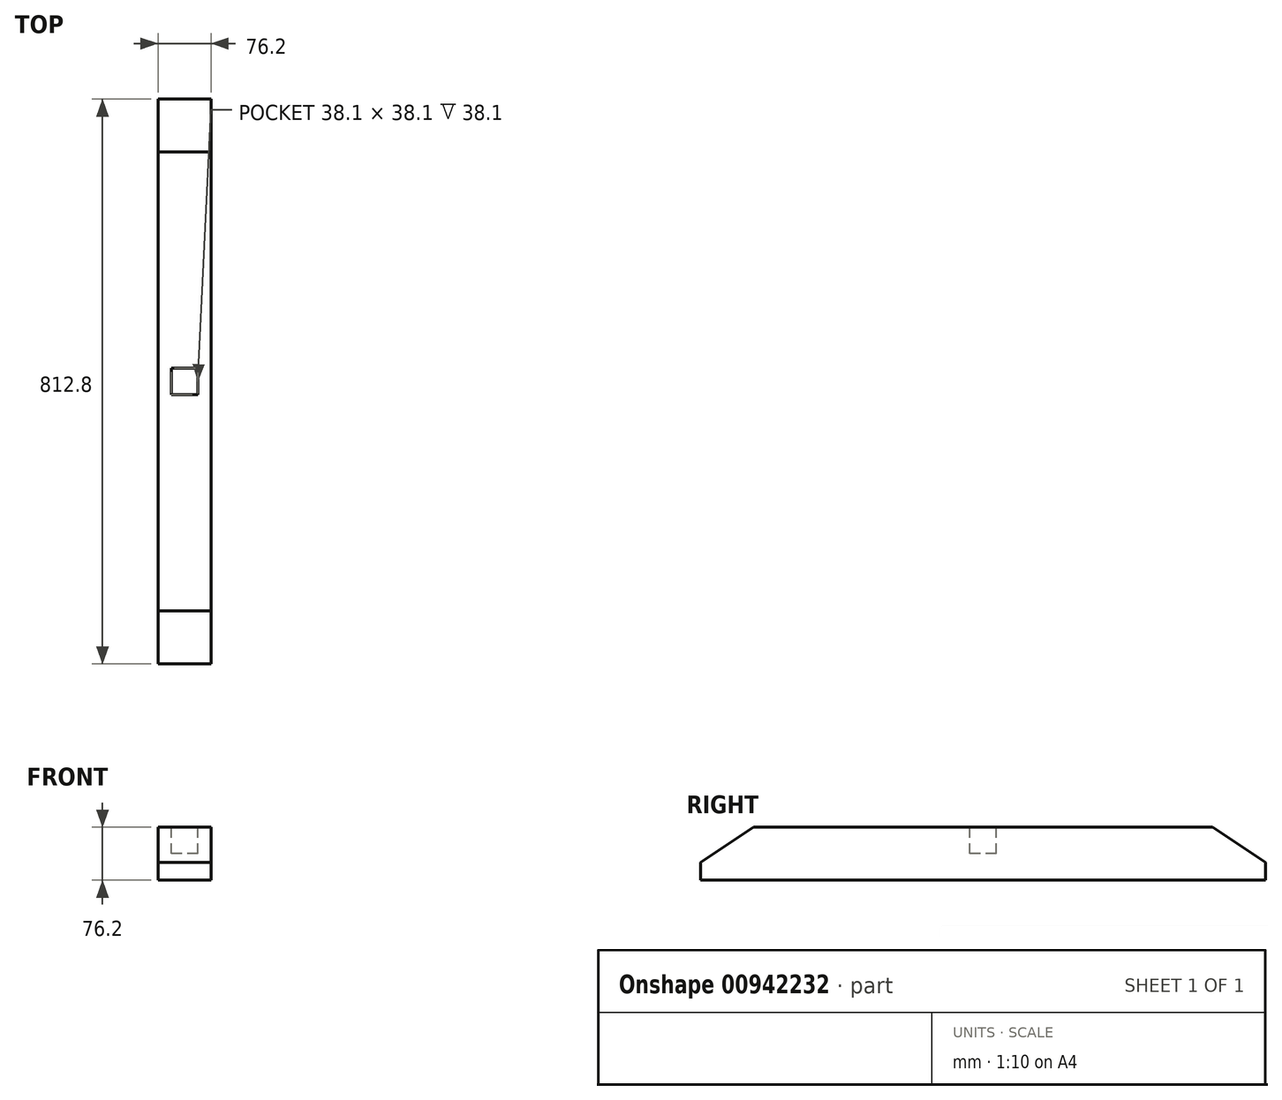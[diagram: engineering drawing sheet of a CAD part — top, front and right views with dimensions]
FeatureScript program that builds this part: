
annotation { "Feature Type Name" : "Feature", "Feature Type Description" : "" }
export const myFeature = defineFeature(function(context is Context, id is Id, definition is map)
    precondition{}
    {
        {
            var Q0;
            Q0=qCreatedBy(makeId("Right.planeOp"),FACE);
            var sketch = newSketch(context, id + "F0", { "sketchPlane" : qUnion([Q0])});
            skLineSegment(sketch, "E0.bottom", {"start": v(330.2, 38.1) * mm, "end": v(-330.2, 38.1) * mm});
            skLineSegment(sketch, "E0.top", {"start": v(406.4, -38.1) * mm, "end": v(292.1, -38.1) * mm});
            skLineSegment(sketch, "E0.left", {"start": v(406.4, -12.7) * mm, "end": v(406.4, -38.1) * mm});
            skLineSegment(sketch, "E0.right", {"start": v(-406.4, -12.7) * mm, "end": v(-406.4, -38.1) * mm});
            skPoint(sketch, "E0.middle", {"position": v(0, 0) * mm});
            skPoint(sketch, "E1.middle", {"position": v(0, -38.1) * mm});
            skLineSegment(sketch, "E2.trimOffspring", {"start": v(-292.1, -38.1) * mm, "end": v(-406.4, -38.1) * mm});
            skPoint(sketch, "E3.orphan", {"position": v(292.1, -57.15) * mm});
            skPoint(sketch, "E4.orphan", {"position": v(-292.1, -57.15) * mm});
            skLineSegment(sketch, "E5", {"start": v(-406.4, -38.1) * mm, "end": v(-406.4, -12.7) * mm});
            skLineSegment(sketch, "E6", {"start": v(-406.4, -12.7) * mm, "end": v(-330.2, 38.1) * mm});
            skLineSegment(sketch, "E7.MirrorCS", {"start": v(406.4, -12.7) * mm, "end": v(330.2, 38.1) * mm});
            skPoint(sketch, "E8.orphan", {"position": v(-406.4, 38.1) * mm});
            skPoint(sketch, "E9.orphan", {"position": v(406.4, 38.1) * mm});
            skLineSegment(sketch, "E10", {"start": v(-292.1, -38.1) * mm, "end": v(292.1, -38.1) * mm});
            skPoint(sketch, "E1.right.start.orphan", {"position": v(-292.1, -19.05) * mm});
            skPoint(sketch, "E1.left.start.orphan", {"position": v(292.1, -19.05) * mm});
            skSolve(sketch);
        }
        {
            var Q0;
            Q0=qSketchRegion(id+"F0",true);
            extrude(context, id + "F1", {"entities" : qUnion([Q0]), "depth" : 76.2 * mm, "offsetDistance" : 25.4 * mm});
        }
        {
            var Q0;
            Q0=makeQuery(id+"F1.opExtrude","SWEPT_FACE",FACE,{"disambiguationData":[OSD([sQuery(id+"F0.wireOp",EDGE,"E0.bottom")])]});
            var sketch = newSketch(context, id + "F2", { "sketchPlane" : qUnion([Q0])});
            skLineSegment(sketch, "E11", {"start": v(0, 0) * mm, "end": v(76.2, 0) * mm});
            skLineSegment(sketch, "E12.bottom", {"start": v(57.15, 19.05) * mm, "end": v(19.05, 19.05) * mm});
            skLineSegment(sketch, "E12.top", {"start": v(57.15, -19.05) * mm, "end": v(19.05, -19.05) * mm});
            skLineSegment(sketch, "E12.left", {"start": v(57.15, 19.05) * mm, "end": v(57.15, -19.05) * mm});
            skLineSegment(sketch, "E12.right", {"start": v(19.05, 19.05) * mm, "end": v(19.05, -19.05) * mm});
            skPoint(sketch, "E12.middle", {"position": v(38.1, 0) * mm});
            skSolve(sketch);
        }
        {
            var Q0;
            Q0=qSketchRegion(id+"F2",true);
            extrude(context, id + "F3", {"entities" : qUnion([Q0]), "operationType" : NewBodyOperationType.REMOVE, "oppositeDirection" : true, "depth" : 38.1 * mm, "offsetDistance" : 25.4 * mm});
        }
    });
